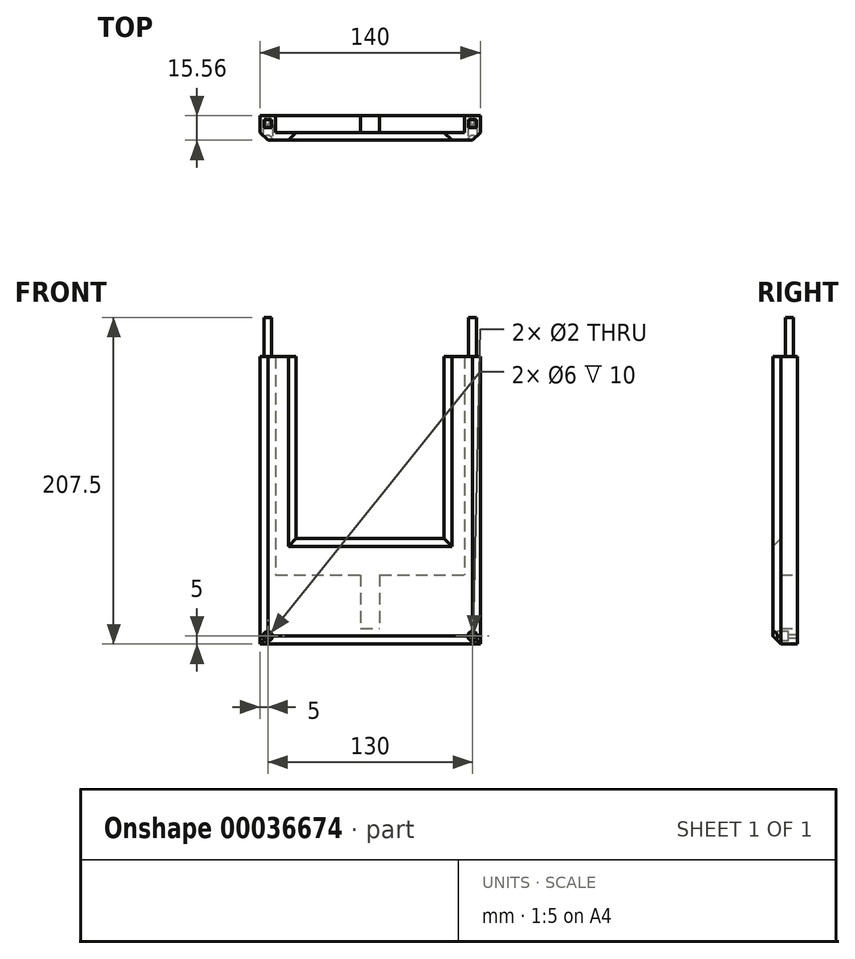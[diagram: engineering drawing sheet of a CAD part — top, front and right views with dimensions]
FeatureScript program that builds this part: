
annotation { "Feature Type Name" : "Feature", "Feature Type Description" : "" }
export const myFeature = defineFeature(function(context is Context, id is Id, definition is map)
    precondition{}
    {
        {
            var Q0;
            Q0=qCreatedBy(makeId("Front.planeOp"),FACE);
            var sketch = newSketch(context, id + "F0", { "sketchPlane" : qUnion([Q0])});
            skLineSegment(sketch, "E0.bottom", {"start": v(0, 0) * mm, "end": v(-140, 0) * mm});
            skLineSegment(sketch, "E0.top", {"start": v(0, 252.5) * mm, "end": v(-140, 252.5) * mm});
            skLineSegment(sketch, "E0.left", {"start": v(0, 0) * mm, "end": v(0, 252.5) * mm});
            skLineSegment(sketch, "E0.right", {"start": v(-140, 0) * mm, "end": v(-140, 252.5) * mm});
            skLineSegment(sketch, "E1.bottom", {"start": v(-130, 242.5) * mm, "end": v(-10, 242.5) * mm});
            skLineSegment(sketch, "E1.top", {"start": v(-130, 44) * mm, "end": v(-10, 44) * mm});
            skLineSegment(sketch, "E1.left", {"start": v(-130, 242.5) * mm, "end": v(-130, 44) * mm});
            skLineSegment(sketch, "E1.right", {"start": v(-10, 242.5) * mm, "end": v(-10, 44) * mm});
            skLineSegment(sketch, "E2.bottom", {"start": v(-117, 219.5) * mm, "end": v(-23, 219.5) * mm});
            skLineSegment(sketch, "E2.top", {"start": v(-117, 67) * mm, "end": v(-23, 67) * mm});
            skLineSegment(sketch, "E2.left", {"start": v(-117, 219.5) * mm, "end": v(-117, 67) * mm});
            skLineSegment(sketch, "E2.right", {"start": v(-23, 219.5) * mm, "end": v(-23, 67) * mm});
            skLineSegment(sketch, "E3.bottom", {"start": v(-76, 44) * mm, "end": v(-64, 44) * mm});
            skLineSegment(sketch, "E3.top", {"start": v(-76, 10) * mm, "end": v(-64, 10) * mm});
            skLineSegment(sketch, "E3.left", {"start": v(-76, 44) * mm, "end": v(-76, 10) * mm});
            skLineSegment(sketch, "E3.right", {"start": v(-64, 44) * mm, "end": v(-64, 10) * mm});
            skCircle(sketch, "E4", {"center": v(-70, 232.5) * mm, "radius": 2.5 * mm});
            skCircle(sketch, "E5", {"center": v(-135, 247.5) * mm, "radius": 1 * mm});
            skLineSegment(sketch, "E6.direction1", {"start": v(-135, 247.5) * mm, "end": v(-5, 247.5) * mm, "construction": true});
            skLineSegment(sketch, "E6.direction2", {"start": v(-135, 247.5) * mm, "end": v(-135, 5) * mm, "construction": true});
            skCircle(sketch, "E7.0.1.0", {"center": v(-135, 5) * mm, "radius": 1 * mm});
            skCircle(sketch, "E7.1.0.0", {"center": v(-5, 247.5) * mm, "radius": 1 * mm});
            skCircle(sketch, "E7.1.1.0", {"center": v(-5, 5) * mm, "radius": 1 * mm});
            skSolve(sketch);
        }
        {
            var Q0;
            Q0=makeQuery(id+"F0.imprint","IMPRINT",FACE,{"disambiguationData":[TD([[makeQuery(id+"F0.imprint","IMPRINT",EDGE,{"derivedFrom":sQuery(id+"F0.wireOp",EDGE,"E0.bottom")}),-1.0]])]});
            var Q1;
            Q1=makeQuery(id+"F0.imprint","IMPRINT",FACE,{"disambiguationData":[TD([[makeQuery(id+"F0.imprint","IMPRINT",EDGE,{"derivedFrom":sQuery(id+"F0.wireOp",EDGE,"E3.top")}),1.0]])]});
            var Q2;
            Q2=makeQuery(id+"F0.imprint","IMPRINT",FACE,{"disambiguationData":[TD([[makeQuery(id+"F0.imprint","IMPRINT",EDGE,{"derivedFrom":sQuery(id+"F0.wireOp",EDGE,"E1.bottom")}),-1.0]])]});
            var Q3;
            Q3=makeQuery(id+"F0.imprint","IMPRINT",FACE,{"disambiguationData":[TD([[makeQuery(id+"F0.imprint","IMPRINT",EDGE,{"derivedFrom":sQuery(id+"F0.wireOp",EDGE,"E6.1.1.0")}),1.0]])]});
            var Q4;
            Q4=makeQuery(id+"F0.imprint","IMPRINT",FACE,{"disambiguationData":[TD([[makeQuery(id+"F0.imprint","IMPRINT",EDGE,{"derivedFrom":sQuery(id+"F0.wireOp",EDGE,"E6.0.1.0")}),1.0]])]});
            var Q5;
            Q5=makeQuery(id+"F0.imprint","IMPRINT",FACE,{"disambiguationData":[TD([[makeQuery(id+"F0.imprint","IMPRINT",EDGE,{"derivedFrom":sQuery(id+"F0.wireOp",EDGE,"E6.1.0.0")}),1.0]])]});
            var Q6;
            Q6=makeQuery(id+"F0.imprint","IMPRINT",FACE,{"disambiguationData":[TD([[makeQuery(id+"F0.imprint","IMPRINT",EDGE,{"derivedFrom":sQuery(id+"F0.wireOp",EDGE,"E0.bottom")}),-1.0]])]});
            extrude(context, id + "F1", {"entities" : qUnion([Q0, Q1, Q2, Q3, Q4, Q5, Q6]), "depth" : (10.56 + 5) * mm});
        }
        {
            var Q0;
            Q0=makeQuery(id+"F0.imprint","IMPRINT",FACE,{"disambiguationData":[TD([[makeQuery(id+"F0.imprint","IMPRINT",EDGE,{"derivedFrom":sQuery(id+"F0.wireOp",EDGE,"E1.bottom")}),-1.0]])]});
            var Q1;
            Q1=makeQuery(id+"F0.imprint","IMPRINT",FACE,{"disambiguationData":[TD([[makeQuery(id+"F0.imprint","IMPRINT",EDGE,{"derivedFrom":sQuery(id+"F0.wireOp",EDGE,"E3.top")}),1.0]])]});
            extrude(context, id + "F2", {"entities" : qUnion([Q0, Q1]), "operationType" : NewBodyOperationType.REMOVE, "depth" : 10.56 * mm});
        }
        {
            var Q0;
            Q0=makeQuery(id+"F1.opExtrude","CAP_EDGE",EDGE,{"disambiguationData":[OSD([sQuery(id+"F0.wireOp",EDGE,"E0.bottom")])],"isStart":false});
            var Q1;
            Q1=makeQuery(id+"F1.opExtrude","CAP_EDGE",EDGE,{"disambiguationData":[OSD([sQuery(id+"F0.wireOp",EDGE,"E0.right")])],"isStart":false});
            var Q2;
            Q2=makeQuery(id+"F1.opExtrude","CAP_EDGE",EDGE,{"disambiguationData":[OSD([sQuery(id+"F0.wireOp",EDGE,"E0.left")])],"isStart":false});
            var Q3;
            Q3=makeQuery(id+"F1.opExtrude","CAP_EDGE",EDGE,{"disambiguationData":[OSD([sQuery(id+"F0.wireOp",EDGE,"E0.top")])],"isStart":false});
            chamfer(context, id + "F3", {"entities" : qUnion([Q0, Q1, Q2, Q3]), "width" : 5 * mm, "tangentPropagation" : true});
        }
        {
            var Q0;
            Q0=makeQuery(id+"F1.opExtrude","CAP_EDGE",EDGE,{"disambiguationData":[OSD([sQuery(id+"F0.wireOp",EDGE,"E4")])],"isStart":false});
            chamfer(context, id + "F4", {"entities" : qUnion([Q0]), "width" : 2.5 * mm, "tangentPropagation" : true});
        }
        {
            var Q0;
            Q0=makeQuery(id+"F1.opExtrude","CAP_FACE",FACE,{"disambiguationData":[OSD([sQuery(id+"F0.wireOp",EDGE,"E0.bottom"),sQuery(id+"F0.wireOp",EDGE,"E0.top"),sQuery(id+"F0.wireOp",EDGE,"E0.left"),sQuery(id+"F0.wireOp",EDGE,"E0.right"),sQuery(id+"F0.wireOp",EDGE,"E2.bottom"),sQuery(id+"F0.wireOp",EDGE,"E2.top"),sQuery(id+"F0.wireOp",EDGE,"E2.left"),sQuery(id+"F0.wireOp",EDGE,"E2.right"),sQuery(id+"F0.wireOp",EDGE,"E4"),sQuery(id+"F0.wireOp",EDGE,"E5"),sQuery(id+"F0.wireOp",EDGE,"E7.0.1.0"),sQuery(id+"F0.wireOp",EDGE,"E7.1.0.0"),sQuery(id+"F0.wireOp",EDGE,"E7.1.1.0")])],"isStart":false});
            var sketch = newSketch(context, id + "F5", { "sketchPlane" : qUnion([Q0])});
            skCircle(sketch, "E8", {"center": v(-135, 247.5) * mm, "radius": 3 * mm});
            skCircle(sketch, "E9.0.1.0", {"center": v(-135, 5) * mm, "radius": 3 * mm});
            skCircle(sketch, "E9.1.0.0", {"center": v(-5, 247.5) * mm, "radius": 3 * mm});
            skCircle(sketch, "E9.1.1.0", {"center": v(-5, 5) * mm, "radius": 3 * mm});
            skLineSegment(sketch, "E9.direction1", {"start": v(-135, 247.5) * mm, "end": v(-5, 247.5) * mm, "construction": true});
            skLineSegment(sketch, "E9.direction2", {"start": v(-135, 247.5) * mm, "end": v(-135, 5) * mm, "construction": true});
            skSolve(sketch);
        }
        {
            var Q0;
            Q0=qSketchRegion(id+"F5",true);
            extrude(context, id + "F6", {"entities" : qUnion([Q0]), "operationType" : NewBodyOperationType.REMOVE, "oppositeDirection" : true, "depth" : 10 * mm});
        }
        {
            var Q0;
            Q0=makeQuery(id+"F1.opExtrude","CAP_EDGE",EDGE,{"disambiguationData":[OSD([sQuery(id+"F0.wireOp",EDGE,"E2.top")])],"isStart":false});
            var Q1;
            Q1=makeQuery(id+"F1.opExtrude","CAP_EDGE",EDGE,{"disambiguationData":[OSD([sQuery(id+"F0.wireOp",EDGE,"E2.left")])],"isStart":false});
            var Q2;
            Q2=makeQuery(id+"F1.opExtrude","CAP_EDGE",EDGE,{"disambiguationData":[OSD([sQuery(id+"F0.wireOp",EDGE,"E2.right")])],"isStart":false});
            var Q3;
            Q3=makeQuery(id+"F1.opExtrude","CAP_EDGE",EDGE,{"disambiguationData":[OSD([sQuery(id+"F0.wireOp",EDGE,"E2.bottom")])],"isStart":false});
            chamfer(context, id + "F7", {"entities" : qUnion([Q0, Q1, Q2, Q3]), "width" : 5 * mm, "tangentPropagation" : true});
        }
        {
            var Q0;
            Q0=makeQuery(id+"F1.opExtrude","CAP_FACE",FACE,{"disambiguationData":[OSD([sQuery(id+"F0.wireOp",EDGE,"E0.bottom"),sQuery(id+"F0.wireOp",EDGE,"E0.top"),sQuery(id+"F0.wireOp",EDGE,"E0.left"),sQuery(id+"F0.wireOp",EDGE,"E0.right"),sQuery(id+"F0.wireOp",EDGE,"E2.bottom"),sQuery(id+"F0.wireOp",EDGE,"E2.top"),sQuery(id+"F0.wireOp",EDGE,"E2.left"),sQuery(id+"F0.wireOp",EDGE,"E2.right"),sQuery(id+"F0.wireOp",EDGE,"E4"),sQuery(id+"F0.wireOp",EDGE,"E5"),sQuery(id+"F0.wireOp",EDGE,"E7.0.1.0"),sQuery(id+"F0.wireOp",EDGE,"E7.1.0.0"),sQuery(id+"F0.wireOp",EDGE,"E7.1.1.0")])],"isStart":false});
            var sketch = newSketch(context, id + "F8", { "sketchPlane" : qUnion([Q0])});
            skLineSegment(sketch, "E10.bottom", {"start": v(5.81, 252.5) * mm, "end": v(-155.44, 252.5) * mm});
            skLineSegment(sketch, "E10.top", {"start": v(5.81, 182.5) * mm, "end": v(-155.44, 182.5) * mm});
            skLineSegment(sketch, "E10.left", {"start": v(5.81, 252.5) * mm, "end": v(5.81, 182.5) * mm});
            skLineSegment(sketch, "E10.right", {"start": v(-155.44, 252.5) * mm, "end": v(-155.44, 182.5) * mm});
            skSolve(sketch);
        }
        {
            var Q0;
            Q0 = qSketchRegion(id + "F8", true);
            extrude(context, id + "F9", {"entities" : qUnion([Q0]), "operationType" : NewBodyOperationType.REMOVE, "oppositeDirection" : true, "depth" : 25 * mm});
        }
        {
            var Q0;
            Q0=makeQuery(id+"F1.opExtrude","CAP_FACE",FACE,{"disambiguationData":[OSD([sQuery(id+"F0.wireOp",EDGE,"E0.bottom"),sQuery(id+"F0.wireOp",EDGE,"E0.top"),sQuery(id+"F0.wireOp",EDGE,"E0.left"),sQuery(id+"F0.wireOp",EDGE,"E0.right"),sQuery(id+"F0.wireOp",EDGE,"E2.bottom"),sQuery(id+"F0.wireOp",EDGE,"E2.top"),sQuery(id+"F0.wireOp",EDGE,"E2.left"),sQuery(id+"F0.wireOp",EDGE,"E2.right"),sQuery(id+"F0.wireOp",EDGE,"E4"),sQuery(id+"F0.wireOp",EDGE,"E5"),sQuery(id+"F0.wireOp",EDGE,"E7.0.1.0"),sQuery(id+"F0.wireOp",EDGE,"E7.1.0.0"),sQuery(id+"F0.wireOp",EDGE,"E7.1.1.0")])],"isStart":true});
            cPlane(context, id + "F10", {"entities" : qUnion([Q0]), "cplaneType" : CPlaneType.OFFSET, "offset" : 2.5 * mm, "oppositeDirection" : true, "width" : 150 * mm, "height" : 150 * mm});
        }
        {
            var Q0;
            Q0=qCreatedBy(id+"F10.planeOp",FACE);
            var sketch = newSketch(context, id + "F11", { "sketchPlane" : qUnion([Q0])});
            skLineSegment(sketch, "E11.bottom", {"start": v(132.5, 157.5) * mm, "end": v(137.5, 157.5) * mm});
            skLineSegment(sketch, "E11.top", {"start": v(132.5, 207.5) * mm, "end": v(137.5, 207.5) * mm});
            skLineSegment(sketch, "E11.left", {"start": v(132.5, 157.5) * mm, "end": v(132.5, 207.5) * mm});
            skLineSegment(sketch, "E11.right", {"start": v(137.5, 157.5) * mm, "end": v(137.5, 207.5) * mm});
            skLineSegment(sketch, "E12.1.0.0", {"start": v(7.5, 157.5) * mm, "end": v(7.5, 207.5) * mm});
            skLineSegment(sketch, "E12.1.0.1", {"start": v(2.5, 157.5) * mm, "end": v(7.5, 157.5) * mm});
            skLineSegment(sketch, "E12.1.0.2", {"start": v(2.5, 157.5) * mm, "end": v(2.5, 207.5) * mm});
            skLineSegment(sketch, "E12.1.0.3", {"start": v(2.5, 207.5) * mm, "end": v(7.5, 207.5) * mm});
            skLineSegment(sketch, "E12.direction1", {"start": v(137.5, 157.5) * mm, "end": v(7.5, 157.5) * mm, "construction": true});
            skSolve(sketch);
        }
        {
            var Q0;
            Q0 = qSketchRegion(id + "F11", true);
            extrude(context, id + "F12", {"entities" : qUnion([Q0]), "operationType" : NewBodyOperationType.ADD, "oppositeDirection" : true, "depth" : 5 * mm});
        }
    });
